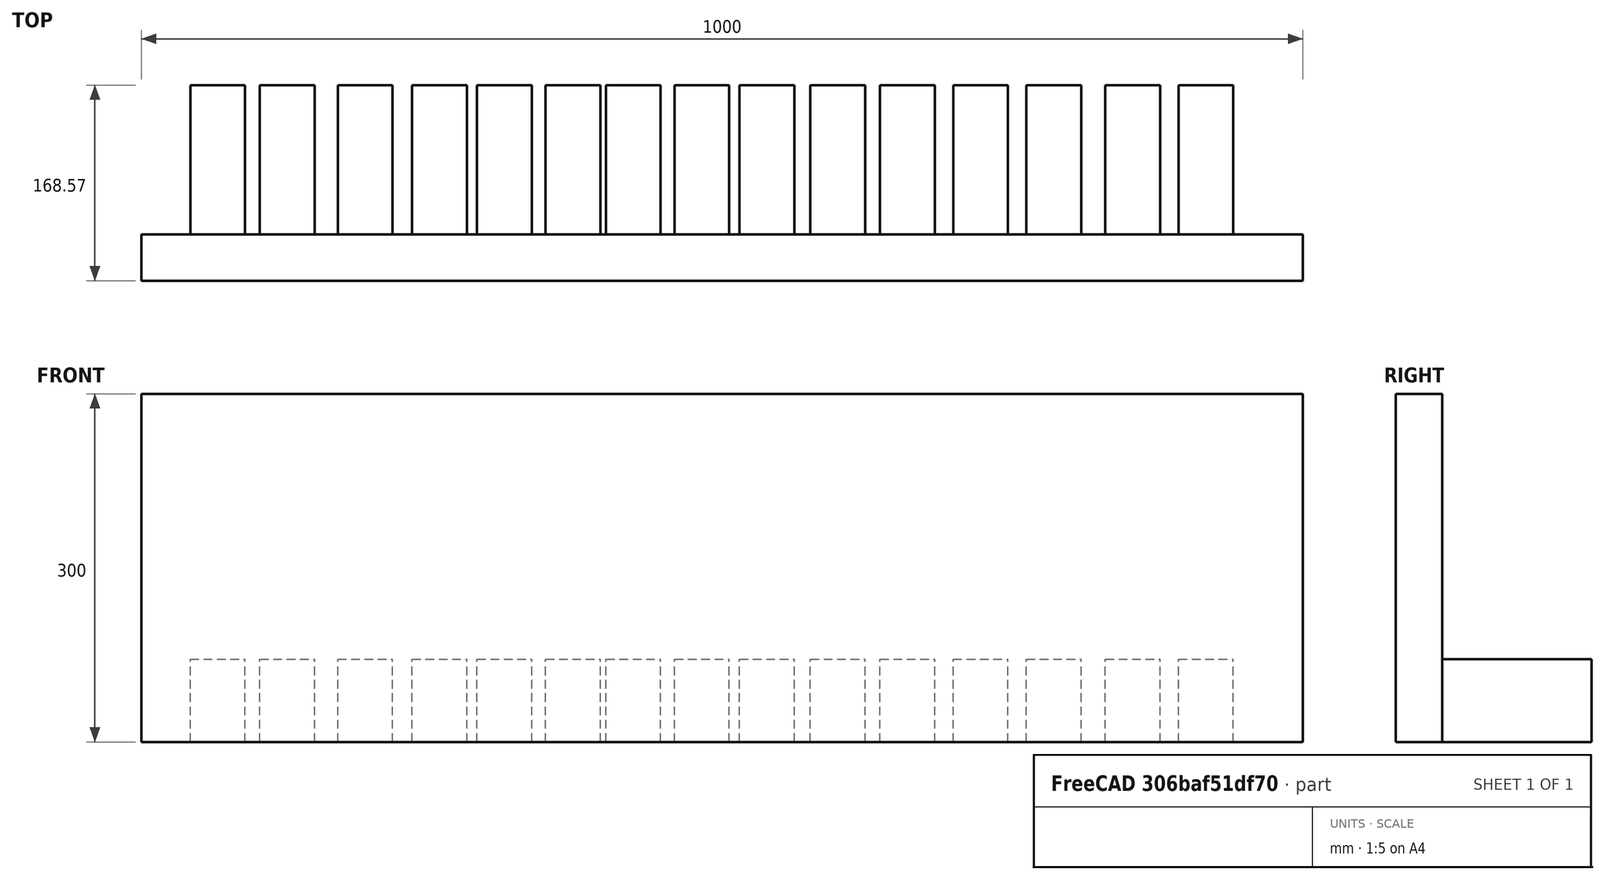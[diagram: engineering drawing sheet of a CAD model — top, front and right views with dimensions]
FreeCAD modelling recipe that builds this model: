
FCSTD DOCUMENT  (FreeCAD 0.18.3R)
Label: moai_stand
License: All rights reserved
LicenseURL: http://en.wikipedia.org/wiki/All_rights_reserved
objects: Part::Box×16, Image::ImagePlane×1
note: 16 computed .brp shape members not serialized (recipe doc carries the construction recipe); baked Part::Feature solids carry a one-line shape summary decoded from their .brp

FEATURE [Image::ImagePlane] ImagePlane
  Placement = pos=(95,114,0) rot=(0,0,1;0rad)
  XSize = 1600
  YSize = 850
  expr: XSize = 800 * 2
  expr: YSize = 425 * 2
FEATURE [Part::Box] Box  label="stand"
  AttacherType = Attacher::AttachEngine3D
  Height = 300
  Length = 1000
  Placement = pos=(-404,-30,0) rot=(0,0,1;0rad)
  Width = 40
FEATURE [Part::Box] Box001  label="moai_rough_001"
  AttacherType = Attacher::AttachEngine3D
  Height = 71.4286
  Length = 47.1429
  Placement = pos=(-362,10,0) rot=(0,0,1;0rad)
  Width = 128.571
  expr: Height = 100 / 1.4
  expr: Length = 66 / 1.4
  expr: Width = 180 / 1.4
FEATURE [Part::Box] Box002  label="moai_rough_002"
  AttacherType = Attacher::AttachEngine3D
  Height = 71.4286
  Length = 47.1429
  Placement = pos=(-302,10,0) rot=(0,0,1;0rad)
  Width = 128.571
  expr: Height = 100 / 1.4
  expr: Length = 66 / 1.4
  expr: Width = 180 / 1.4
FEATURE [Part::Box] Box003  label="moai_rough_003"
  AttacherType = Attacher::AttachEngine3D
  Height = 71.4286
  Length = 47.1429
  Placement = pos=(-235,10,0) rot=(0,0,1;0rad)
  Width = 128.571
  expr: Height = 100 / 1.4
  expr: Length = 66 / 1.4
  expr: Width = 180 / 1.4
FEATURE [Part::Box] Box004  label="moai_rough_004"
  AttacherType = Attacher::AttachEngine3D
  Height = 71.4286
  Length = 47.1429
  Placement = pos=(-171,10,0) rot=(0,0,1;0rad)
  Width = 128.571
  expr: Height = 100 / 1.4
  expr: Length = 66 / 1.4
  expr: Width = 180 / 1.4
FEATURE [Part::Box] Box005  label="moai_rough_005"
  AttacherType = Attacher::AttachEngine3D
  Height = 71.4286
  Length = 47.1429
  Placement = pos=(-115,10,0) rot=(0,0,1;0rad)
  Width = 128.571
  expr: Height = 100 / 1.4
  expr: Length = 66 / 1.4
  expr: Width = 180 / 1.4
FEATURE [Part::Box] Box006  label="moai_rough_006"
  AttacherType = Attacher::AttachEngine3D
  Height = 71.4286
  Length = 47.1429
  Placement = pos=(-56,10,0) rot=(0,0,1;0rad)
  Width = 128.571
  expr: Height = 100 / 1.4
  expr: Length = 66 / 1.4
  expr: Width = 180 / 1.4
FEATURE [Part::Box] Box007  label="moai_rough_007"
  AttacherType = Attacher::AttachEngine3D
  Height = 71.4286
  Length = 47.1429
  Placement = pos=(-4,10,0) rot=(0,0,1;0rad)
  Width = 128.571
  expr: Height = 100 / 1.4
  expr: Length = 66 / 1.4
  expr: Width = 180 / 1.4
FEATURE [Part::Box] Box008  label="moai_rough_008"
  AttacherType = Attacher::AttachEngine3D
  Height = 71.4286
  Length = 47.1429
  Placement = pos=(55,10,0) rot=(0,0,1;0rad)
  Width = 128.571
  expr: Height = 100 / 1.4
  expr: Length = 66 / 1.4
  expr: Width = 180 / 1.4
FEATURE [Part::Box] Box009  label="moai_rough_009"
  AttacherType = Attacher::AttachEngine3D
  Height = 71.4286
  Length = 47.1429
  Placement = pos=(111,10,0) rot=(0,0,1;0rad)
  Width = 128.571
  expr: Height = 100 / 1.4
  expr: Length = 66 / 1.4
  expr: Width = 180 / 1.4
FEATURE [Part::Box] Box010  label="moai_rough_010"
  AttacherType = Attacher::AttachEngine3D
  Height = 71.4286
  Length = 47.1429
  Placement = pos=(172,10,0) rot=(0,0,1;0rad)
  Width = 128.571
  expr: Height = 100 / 1.4
  expr: Length = 66 / 1.4
  expr: Width = 180 / 1.4
FEATURE [Part::Box] Box011  label="moai_rough_011"
  AttacherType = Attacher::AttachEngine3D
  Height = 71.4286
  Length = 47.1429
  Placement = pos=(232,10,0) rot=(0,0,1;0rad)
  Width = 128.571
  expr: Height = 100 / 1.4
  expr: Length = 66 / 1.4
  expr: Width = 180 / 1.4
FEATURE [Part::Box] Box012  label="moai_rough_012"
  AttacherType = Attacher::AttachEngine3D
  Height = 71.4286
  Length = 47.1429
  Placement = pos=(295,10,0) rot=(0,0,1;0rad)
  Width = 128.571
  expr: Height = 100 / 1.4
  expr: Length = 66 / 1.4
  expr: Width = 180 / 1.4
FEATURE [Part::Box] Box013  label="moai_rough_013"
  AttacherType = Attacher::AttachEngine3D
  Height = 71.4286
  Length = 47.1429
  Placement = pos=(358,10,0) rot=(0,0,1;0rad)
  Width = 128.571
  expr: Height = 100 / 1.4
  expr: Length = 66 / 1.4
  expr: Width = 180 / 1.4
FEATURE [Part::Box] Box014  label="moai_rough_014"
  AttacherType = Attacher::AttachEngine3D
  Height = 71.4286
  Length = 47.1429
  Placement = pos=(426,10,0) rot=(0,0,1;0rad)
  Width = 128.571
  expr: Height = 100 / 1.4
  expr: Length = 66 / 1.4
  expr: Width = 180 / 1.4
FEATURE [Part::Box] Box015  label="moai_rough_015"
  AttacherType = Attacher::AttachEngine3D
  Height = 71.4286
  Length = 47.1429
  Placement = pos=(489,10,0) rot=(0,0,1;0rad)
  Width = 128.571
  expr: Height = 100 / 1.4
  expr: Length = 66 / 1.4
  expr: Width = 180 / 1.4
